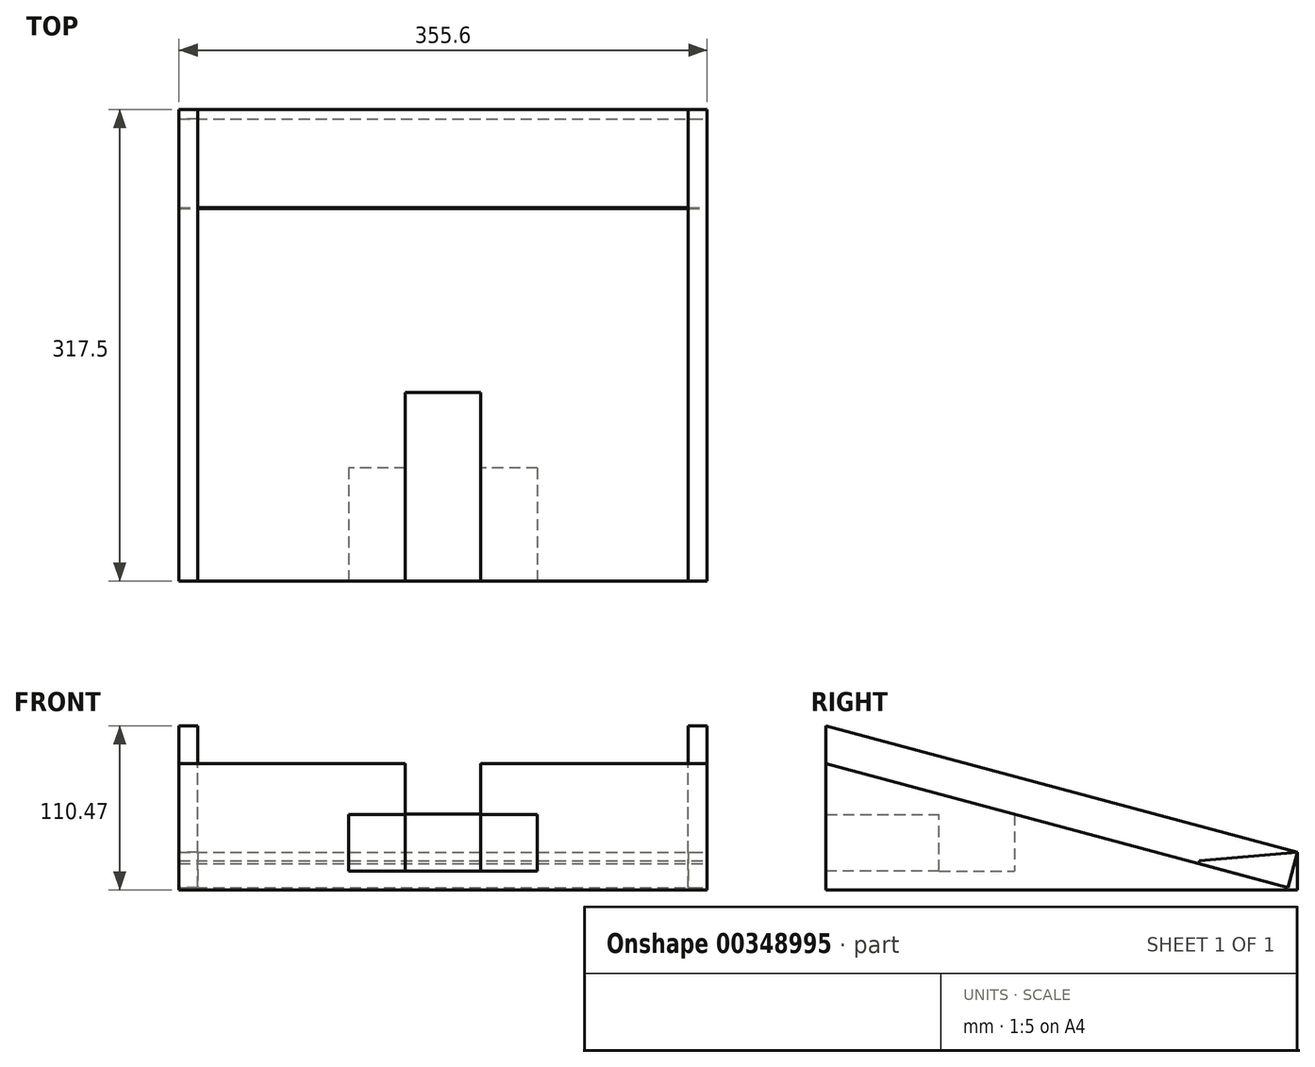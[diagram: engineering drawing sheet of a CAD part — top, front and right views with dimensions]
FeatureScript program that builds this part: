
annotation { "Feature Type Name" : "Feature", "Feature Type Description" : "" }
export const myFeature = defineFeature(function(context is Context, id is Id, definition is map)
    precondition{}
    {
        {
            var Q0;
            Q0=qCreatedBy(makeId("Right.planeOp"),FACE);
            var sketch = newSketch(context, id + "F0", { "sketchPlane" : qUnion([Q0])});
            skLineSegment(sketch, "E0", {"start": v(0, 0) * mm, "end": v(317.5, 0) * mm});
            skLineSegment(sketch, "E1", {"start": v(317.5, 0) * mm, "end": v(0, 85.07) * mm});
            skLineSegment(sketch, "E2", {"start": v(0, 85.07) * mm, "end": v(0, 0) * mm});
            skSolve(sketch);
        }
        {
            var Q0;
            Q0 = qSketchRegion(id + "F0", true);
            extrude(context, id + "F1", {"entities" : qUnion([Q0]), "oppositeDirection" : true, "depth" : 381 * mm});
        }
        {
            var Q0;
            Q0=makeQuery(id+"F1.opExtrude","SWEPT_FACE",FACE,{"disambiguationData":[OSD([sQuery(id+"F0.wireOp",EDGE,"E0")])]});
            var sketch = newSketch(context, id + "F2", { "sketchPlane" : qUnion([Q0])});
            skLineSegment(sketch, "E3.bottom", {"start": v(-215.9, 0) * mm, "end": v(-165.1, 0) * mm});
            skLineSegment(sketch, "E3.top", {"start": v(-215.9, -127) * mm, "end": v(-165.1, -127) * mm});
            skLineSegment(sketch, "E3.left", {"start": v(-215.9, 0) * mm, "end": v(-215.9, -127) * mm});
            skLineSegment(sketch, "E3.right", {"start": v(-165.1, 0) * mm, "end": v(-165.1, -127) * mm});
            skSolve(sketch);
        }
        {
            var Q0;
            Q0 = qSketchRegion(id + "F2", true);
            extrude(context, id + "F3", {"entities" : qUnion([Q0]), "operationType" : NewBodyOperationType.REMOVE, "endBound" : BoundingType.THROUGH_ALL, "oppositeDirection" : true, "depth" : 25.4 * mm, "hasSecondDirection" : true, "secondDirectionOppositeDirection" : true, "secondDirectionDepth" : 12.7 * mm});
        }
        {
            var Q0;
            Q0=makeQuery(id+"F1.opExtrude","SWEPT_FACE",FACE,{"disambiguationData":[OSD([sQuery(id+"F0.wireOp",EDGE,"E2")])]});
            var sketch = newSketch(context, id + "F4", { "sketchPlane" : qUnion([Q0])});
            skLineSegment(sketch, "E4.bottom", {"start": v(-127, 12.7) * mm, "end": v(-254, 12.7) * mm});
            skLineSegment(sketch, "E4.top", {"start": v(-127, 50.8) * mm, "end": v(-254, 50.8) * mm});
            skLineSegment(sketch, "E4.left", {"start": v(-127, 12.7) * mm, "end": v(-127, 50.8) * mm});
            skLineSegment(sketch, "E4.right", {"start": v(-254, 12.7) * mm, "end": v(-254, 50.8) * mm});
            skSolve(sketch);
        }
        {
            var Q0;
            Q0 = qSketchRegion(id + "F4", true);
            extrude(context, id + "F5", {"entities" : qUnion([Q0]), "operationType" : NewBodyOperationType.REMOVE, "oppositeDirection" : true, "depth" : 76.2 * mm});
        }
        {
            var Q0;
            Q0=makeQuery(id+"F1.opExtrude","CAP_FACE",FACE,{"disambiguationData":[OSD([sQuery(id+"F0.wireOp",EDGE,"E0"),sQuery(id+"F0.wireOp",EDGE,"E1"),sQuery(id+"F0.wireOp",EDGE,"E2")])],"isStart":true});
            var sketch = newSketch(context, id + "F6", { "sketchPlane" : qUnion([Q0])});
            skLineSegment(sketch, "E5", {"start": v(317.5, 0) * mm, "end": v(317.5, 25.4) * mm});
            skLineSegment(sketch, "E6", {"start": v(317.5, 25.4) * mm, "end": v(311.15, 1.7) * mm});
            skLineSegment(sketch, "E7", {"start": v(311.15, 1.7) * mm, "end": v(317.5, 0) * mm});
            skSolve(sketch);
        }
        {
            var Q0;
            Q0 = qSketchRegion(id + "F6", true);
            extrude(context, id + "F7", {"entities" : qUnion([Q0]), "operationType" : NewBodyOperationType.ADD, "oppositeDirection" : true, "depth" : 381 * mm});
        }
        {
            var Q0;
            Q0=makeQuery(id+"F7.boolean.opBoolean","MERGE",FACE,{"derivedFrom":[makeQuery(id+"F1.opExtrude","CAP_FACE",FACE,{"disambiguationData":[OSD([sQuery(id+"F0.wireOp",EDGE,"E0"),sQuery(id+"F0.wireOp",EDGE,"E1"),sQuery(id+"F0.wireOp",EDGE,"E2")])],"isStart":true}),makeQuery(id+"F7.opExtrude","CAP_FACE",FACE,{"disambiguationData":[OSD([sQuery(id+"F6.wireOp",EDGE,"E5"),sQuery(id+"F6.wireOp",EDGE,"E6"),sQuery(id+"F6.wireOp",EDGE,"E7")])],"isStart":true})]});
            var sketch = newSketch(context, id + "F8", { "sketchPlane" : qUnion([Q0])});
            skLineSegment(sketch, "E8", {"start": v(317.5, 25.4) * mm, "end": v(0, 110.47) * mm});
            skLineSegment(sketch, "E9", {"start": v(0, 110.47) * mm, "end": v(0, 85.07) * mm});
            skLineSegment(sketch, "E10", {"start": v(0, 85.07) * mm, "end": v(311.15, 1.7) * mm});
            skLineSegment(sketch, "E11", {"start": v(311.15, 1.7) * mm, "end": v(317.5, 25.4) * mm});
            skSolve(sketch);
        }
        {
            var Q0;
            Q0 = qSketchRegion(id + "F8", true);
            extrude(context, id + "F9", {"entities" : qUnion([Q0]), "oppositeDirection" : true, "depth" : 25.4 * mm});
        }
        {
            var Q0;
            Q0=makeQuery(id+"F7.boolean.opBoolean","MERGE",FACE,{"derivedFrom":[makeQuery(id+"F1.opExtrude","CAP_FACE",FACE,{"disambiguationData":[OSD([sQuery(id+"F0.wireOp",EDGE,"E0"),sQuery(id+"F0.wireOp",EDGE,"E1"),sQuery(id+"F0.wireOp",EDGE,"E2")])],"isStart":false}),makeQuery(id+"F7.opExtrude","CAP_FACE",FACE,{"disambiguationData":[OSD([sQuery(id+"F6.wireOp",EDGE,"E5"),sQuery(id+"F6.wireOp",EDGE,"E6"),sQuery(id+"F6.wireOp",EDGE,"E7")])],"isStart":false})]});
            var sketch = newSketch(context, id + "F10", { "sketchPlane" : qUnion([Q0])});
            skLineSegment(sketch, "E12", {"start": v(-317.5, 25.4) * mm, "end": v(0, 110.47) * mm});
            skLineSegment(sketch, "E13", {"start": v(0, 110.47) * mm, "end": v(0, 85.07) * mm});
            skLineSegment(sketch, "E14", {"start": v(0, 85.07) * mm, "end": v(-311.15, 1.7) * mm});
            skLineSegment(sketch, "E15", {"start": v(-311.15, 1.7) * mm, "end": v(-317.5, 25.4) * mm});
            skSolve(sketch);
        }
        {
            var Q0;
            Q0 = qSketchRegion(id + "F10", true);
            extrude(context, id + "F11", {"entities" : qUnion([Q0]), "oppositeDirection" : true, "depth" : 25.4 * mm});
        }
        {
            var Q0;
            Q0=makeQuery(id+"F7.boolean.opBoolean","MERGE",FACE,{"derivedFrom":[makeQuery(id+"F1.opExtrude","CAP_FACE",FACE,{"disambiguationData":[OSD([sQuery(id+"F0.wireOp",EDGE,"E0"),sQuery(id+"F0.wireOp",EDGE,"E1"),sQuery(id+"F0.wireOp",EDGE,"E2")])],"isStart":false}),makeQuery(id+"F7.opExtrude","CAP_FACE",FACE,{"disambiguationData":[OSD([sQuery(id+"F6.wireOp",EDGE,"E5"),sQuery(id+"F6.wireOp",EDGE,"E6"),sQuery(id+"F6.wireOp",EDGE,"E7")])],"isStart":false})]});
            var sketch = newSketch(context, id + "F12", { "sketchPlane" : qUnion([Q0])});
            skLineSegment(sketch, "E16", {"start": v(-317.5, 0) * mm, "end": v(-317.5, 25.4) * mm});
            skLineSegment(sketch, "E17", {"start": v(-317.5, 25.4) * mm, "end": v(0, 110.47) * mm});
            skLineSegment(sketch, "E18", {"start": v(0, 110.47) * mm, "end": v(0, 0) * mm});
            skLineSegment(sketch, "E19", {"start": v(0, 0) * mm, "end": v(-317.5, 0) * mm});
            skSolve(sketch);
        }
        {
            var Q0;
            Q0 = qSketchRegion(id + "F12", true);
            extrude(context, id + "F13", {"entities" : qUnion([Q0]), "operationType" : NewBodyOperationType.REMOVE, "oppositeDirection" : true, "depth" : 12.7 * mm});
        }
        {
            var Q0;
            Q0=makeQuery(id+"F7.boolean.opBoolean","MERGE",FACE,{"derivedFrom":[makeQuery(id+"F1.opExtrude","CAP_FACE",FACE,{"disambiguationData":[OSD([sQuery(id+"F0.wireOp",EDGE,"E0"),sQuery(id+"F0.wireOp",EDGE,"E1"),sQuery(id+"F0.wireOp",EDGE,"E2")])],"isStart":true}),makeQuery(id+"F7.opExtrude","CAP_FACE",FACE,{"disambiguationData":[OSD([sQuery(id+"F6.wireOp",EDGE,"E5"),sQuery(id+"F6.wireOp",EDGE,"E6"),sQuery(id+"F6.wireOp",EDGE,"E7")])],"isStart":true})]});
            var sketch = newSketch(context, id + "F14", { "sketchPlane" : qUnion([Q0])});
            skLineSegment(sketch, "E20", {"start": v(317.5, 0) * mm, "end": v(317.5, 25.4) * mm});
            skLineSegment(sketch, "E21", {"start": v(317.5, 25.4) * mm, "end": v(0, 110.47) * mm});
            skLineSegment(sketch, "E22", {"start": v(0, 110.47) * mm, "end": v(0, 0) * mm});
            skLineSegment(sketch, "E23", {"start": v(0, 0) * mm, "end": v(317.5, 0) * mm});
            skSolve(sketch);
        }
        {
            var Q0;
            Q0 = qSketchRegion(id + "F14", true);
            extrude(context, id + "F15", {"entities" : qUnion([Q0]), "operationType" : NewBodyOperationType.REMOVE, "oppositeDirection" : true, "depth" : 12.7 * mm});
        }
        {
            var Q0;
            Q0=makeQuery(id+"F15.boolean.opBoolean","COPY",FACE,{"disambiguationData":[TD([makeQuery(id+"F1.opExtrude","SWEPT_FACE",FACE,{"disambiguationData":[OSD([sQuery(id+"F0.wireOp",EDGE,"E0")])]})])],"derivedFrom":makeQuery(id+"F15.opExtrude","CAP_FACE",FACE,{"disambiguationData":[OSD([sQuery(id+"F14.wireOp",EDGE,"E20"),sQuery(id+"F14.wireOp",EDGE,"E21"),sQuery(id+"F14.wireOp",EDGE,"E22"),sQuery(id+"F14.wireOp",EDGE,"E23")])],"isStart":false})});
            var sketch = newSketch(context, id + "F16", { "sketchPlane" : qUnion([Q0])});
            skLineSegment(sketch, "E24", {"start": v(317.5, 25.4) * mm, "end": v(251.42, 19.62) * mm});
            skLineSegment(sketch, "E25", {"start": v(311.15, 1.7) * mm, "end": v(317.5, 25.4) * mm});
            skLineSegment(sketch, "E26", {"start": v(250.95, 17.83) * mm, "end": v(311.15, 1.7) * mm});
            skLineSegment(sketch, "E27", {"start": v(250.95, 17.83) * mm, "end": v(251.42, 19.62) * mm});
            skSolve(sketch);
        }
        {
            var Q0;
            Q0 = qSketchRegion(id + "F16", true);
            extrude(context, id + "F17", {"entities" : qUnion([Q0]), "oppositeDirection" : true, "depth" : 355.6 * mm});
        }
    });
